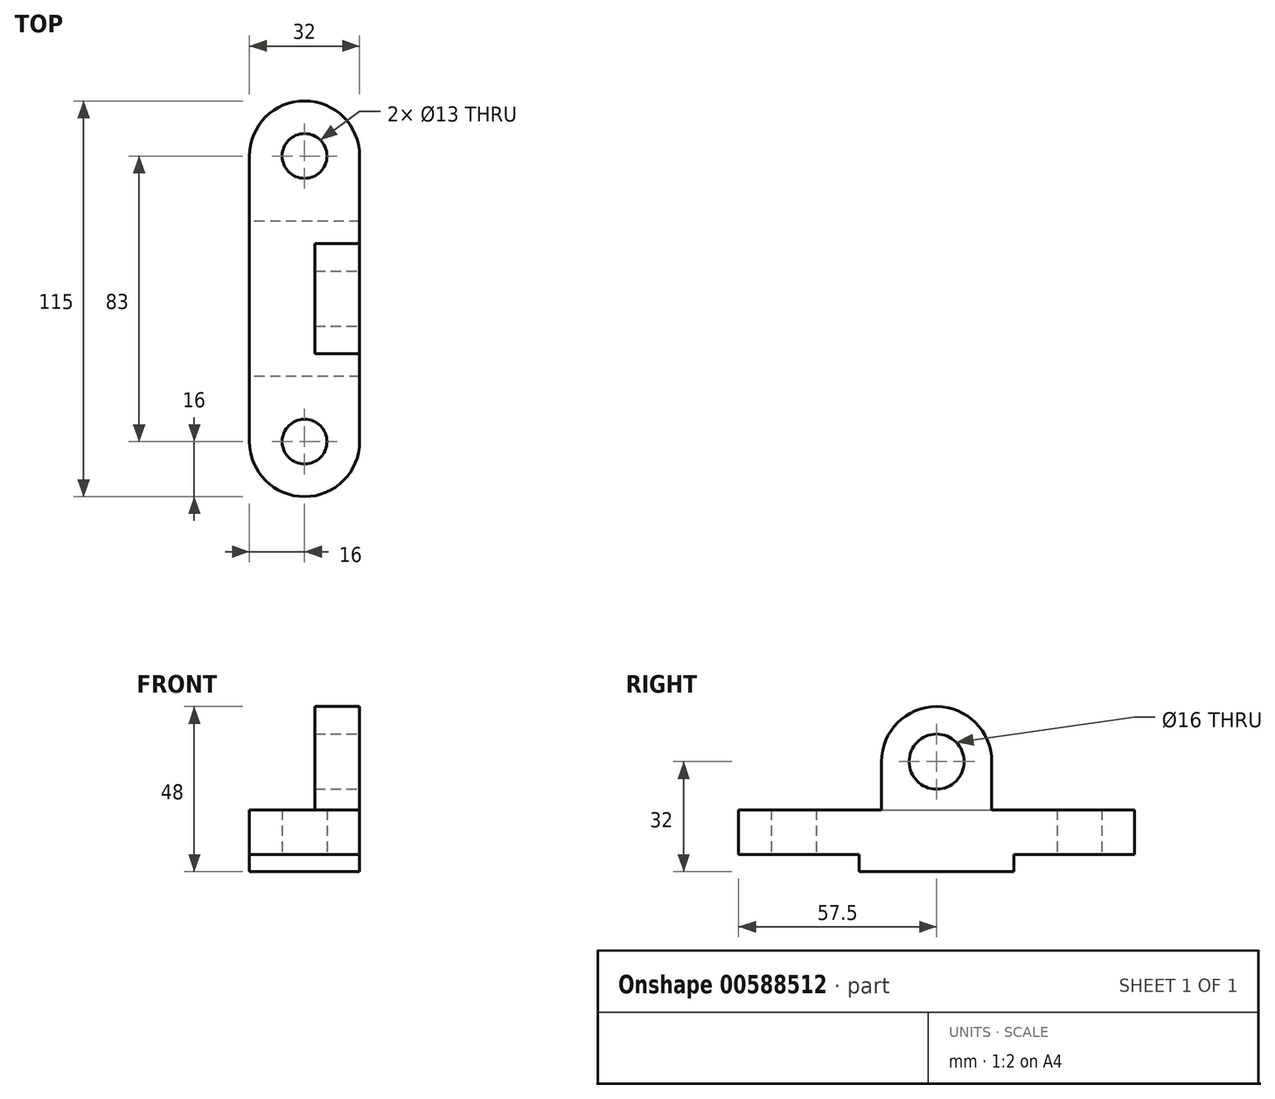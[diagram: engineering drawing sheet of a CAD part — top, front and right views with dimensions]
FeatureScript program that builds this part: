
annotation { "Feature Type Name" : "Feature", "Feature Type Description" : "" }
export const myFeature = defineFeature(function(context is Context, id is Id, definition is map)
    precondition{}
    {
        {
            var Q0;
            Q0=qCreatedBy(makeId("Top.planeOp"),FACE);
            var sketch = newSketch(context, id + "F0", { "sketchPlane" : qUnion([Q0])});
            skArc(sketch, "E0", {"start": v(-16, 0) * mm, "mid": v(0, -16) * mm, "end": v(16, 0) * mm});
            skCircle(sketch, "E1", {"center": v(0, 0) * mm, "radius": 6.5 * mm});
            skCircle(sketch, "E2", {"center": v(0, 83) * mm, "radius": 6.5 * mm});
            skArc(sketch, "E3", {"start": v(16, 83) * mm, "mid": v(0, 99) * mm, "end": v(-16, 83) * mm});
            skLineSegment(sketch, "E4", {"start": v(-16, 0) * mm, "end": v(-16, 83) * mm});
            skLineSegment(sketch, "E5", {"start": v(16, 0) * mm, "end": v(16, 83) * mm});
            skLineSegment(sketch, "E6.bottom", {"start": v(16, 64) * mm, "end": v(-16, 64) * mm});
            skLineSegment(sketch, "E6.top", {"start": v(16, 19) * mm, "end": v(-16, 19) * mm});
            skLineSegment(sketch, "E6.left", {"start": v(16, 64) * mm, "end": v(16, 19) * mm});
            skLineSegment(sketch, "E6.right", {"start": v(-16, 64) * mm, "end": v(-16, 19) * mm});
            skSolve(sketch);
        }
        {
            var Q0;
            Q0=makeQuery(id+"F0.imprint","IMPRINT",FACE,{"disambiguationData":[TD([[makeQuery(id+"F0.imprint","IMPRINT",EDGE,{"derivedFrom":sQuery(id+"F0.wireOp",EDGE,"E6.bottom")}),1.0]])]});
            var Q1;
            {var subQ1=sQuery(id+"F0.wireOp",EDGE,"E0");Q1=makeQuery(id+"F0.imprint","IMPRINT",FACE,{"disambiguationData":[TD([[makeQuery(id+"F0.imprint","IMPRINT",EDGE,{"derivedFrom":subQ1}),1.0]])]});}
            var Q2;
            Q2=makeQuery(id+"F0.imprint","IMPRINT",FACE,{"disambiguationData":[TD([[makeQuery(id+"F0.imprint","IMPRINT",EDGE,{"derivedFrom":sQuery(id+"F0.wireOp",EDGE,"E2")}),-1.0]])]});
            extrude(context, id + "F1", {"entities" : qUnion([Q0, Q1, Q2]), "depth" : 13 * mm, "offsetDistance" : 25 * mm});
        }
        {
            var Q0;
            Q0=makeQuery(id+"F0.imprint","IMPRINT",FACE,{"disambiguationData":[TD([[makeQuery(id+"F0.imprint","IMPRINT",EDGE,{"derivedFrom":sQuery(id+"F0.wireOp",EDGE,"E6.bottom")}),1.0]])]});
            extrude(context, id + "F2", {"entities" : qUnion([Q0]), "operationType" : NewBodyOperationType.ADD, "oppositeDirection" : true, "depth" : 5 * mm, "offsetDistance" : 25 * mm});
        }
        {
            var Q0;
            {var subQ0=sQuery(id+"F0.wireOp",EDGE,"E6.left");Q0=makeQuery(id+"F2.boolean.opBoolean","MERGE",FACE,{"derivedFrom":[makeQuery(id+"F1.opExtrude","SWEPT_FACE",FACE,{"disambiguationData":[OSD([sQuery(id+"F0.wireOp",EDGE,"E5"),subQ0])]}),makeQuery(id+"F2.opExtrude","SWEPT_FACE",FACE,{"disambiguationData":[OSD([subQ0])]})]});}
            var sketch = newSketch(context, id + "F3", { "sketchPlane" : qUnion([Q0])});
            skCircle(sketch, "E7", {"center": v(41.5, 27) * mm, "radius": 8 * mm});
            skArc(sketch, "E8", {"start": v(57.5, 27) * mm, "mid": v(41.5, 43) * mm, "end": v(25.5, 27) * mm});
            skLineSegment(sketch, "E9", {"start": v(25.5, 27) * mm, "end": v(25.5, 13) * mm});
            skLineSegment(sketch, "E10", {"start": v(57.5, 27) * mm, "end": v(57.5, 13) * mm});
            skLineSegment(sketch, "E11", {"start": v(25.5, 13) * mm, "end": v(57.5, 13) * mm});
            skSolve(sketch);
        }
        {
            var Q0;
            Q0=makeQuery(id+"F3.imprint","IMPRINT",FACE,{"disambiguationData":[TD([[makeQuery(id+"F3.imprint","IMPRINT",EDGE,{"derivedFrom":sQuery(id+"F3.wireOp",EDGE,"E7")}),-1.0]])]});
            extrude(context, id + "F4", {"entities" : qUnion([Q0]), "operationType" : NewBodyOperationType.ADD, "oppositeDirection" : true, "depth" : 13 * mm, "offsetDistance" : 25 * mm});
        }
    });
